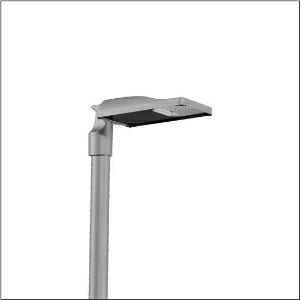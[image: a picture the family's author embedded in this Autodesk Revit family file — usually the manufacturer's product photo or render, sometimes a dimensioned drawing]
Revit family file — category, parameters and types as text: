
# Revit family: streetlight_sl_31_micro___st1_0a_5xh1d71b08da_111b
name_source: partatom
category: Lighting Fixtures
units: mm (PartAtom-declared; Revit-internal decimal feet)

## family parameters
Cut with Voids When Loaded = No
Host = Face
Light Source = No
Part Type = Normal
Room Calculation Point = No
Round Connector Dimension = Use Diameter
Shared = No

## types (1)
- --- (1 x LED, 3800 lm, 35.5 W, 2200K)
    Apparent Load = 36 VA
    CIE Flux Codes = 37 72 97 100 100
    Color Rendering = 70
    Color Temperature = 2200K
    Default Elevation = 1800 mm
    Description = Streetlight SL 31 micro Easy, LST, Desk-Remote mast luminaire for post-top, side-entry; light control with lens of PMMA; light distribution: ST1.0a, direct asymmetric distribution, for standard-compliant lighting for roads and squares; LED: luminous flux: 3.800lm, light colour: 722, colour temperature: 2200K; luminous efficacy: 107lm/W; control: pre-setting: linear dimming characteristic, flexible luminous flux parameterisation, time-dependent luminous flux control, constant luminous flux control, power reduction, intelligent temperature release in ECG and LED module, overheat protection; luminaire housing, of diecast aluminium, SITECO metallic grey (DB 702S), corrosivity category C5 high according to DIN EN ISO 12944; cover of toughened safety glass, transparent, mast flange of diecast aluminium, SITECO metallic grey (DB 702S), spigot size: 76/60mm, mast flange included unmounted; cable length: 6,5m, connection cable pre-assembled; mains connection: 220..240V, AC, 50/60Hz; power consumption (at start of service life): 35,5W / (at end of service life): 37,5W / (with reduced operation 50%): 15,4W; protection rating (complete): IP66; insulation class (complete): insulation class II (safety insulation); impact resistance: IK10; certification: CE, ENEC, ENEC+, VDE, UKCA; permissible operating ambient temperature for outdoor applications: -40..+50°C; packaging unit: 1 piece

Light Distribution: ST1.0a
    Height = 76 mm
    Lamp = 1 x LED
    Lamp Light Flux = 3800 lm
    Lamp Power = 35.5 W
    Lamp count = 1
    Length = 467 mm
    Luminous efficacy = 107 lm/W
    Manufacturer = Siteco
    ModVariant = No
    Model = 5XH1D71B08DA
    Number of Poles = 1
    OnlyDefault = Yes
    Power Factor = 1
    Product Name = Streetlight SL 31 micro | ST1.0a
    Product group = mast luminaire | pylon top
    ProductGroupID = 6100
    Protection Class = Protection class II
    Protection Degree = IP 66
    RLX_Detail_Level = 1
    RLX_Emergency_Light_Flux = 0 lm
    RLX_Emergency_Type = 0
    RLX_Emergency_Type_DB = No
    RlxData = <blob elided: 23157 chars, md5=9c6e8a85>
    Socket = socket
    Standby Power = 0 W
    System Light Flux = 3800 lm
    System Power = 36 W
    Type Comments = factory setting: luminous flux: 100 % | dim-lin: 254 | 700 mA
    Type Image = l_1300309.jpg
    URL = http://relux.com
    VarID = @adj_009593
    Voltage = 0 V
    Weight = 0.00 kg
    Width = 265 mm

## geometry (parser evidence)
native form markers: Blend x4, Sweep x10
no freeform markers — native parametric forms only
